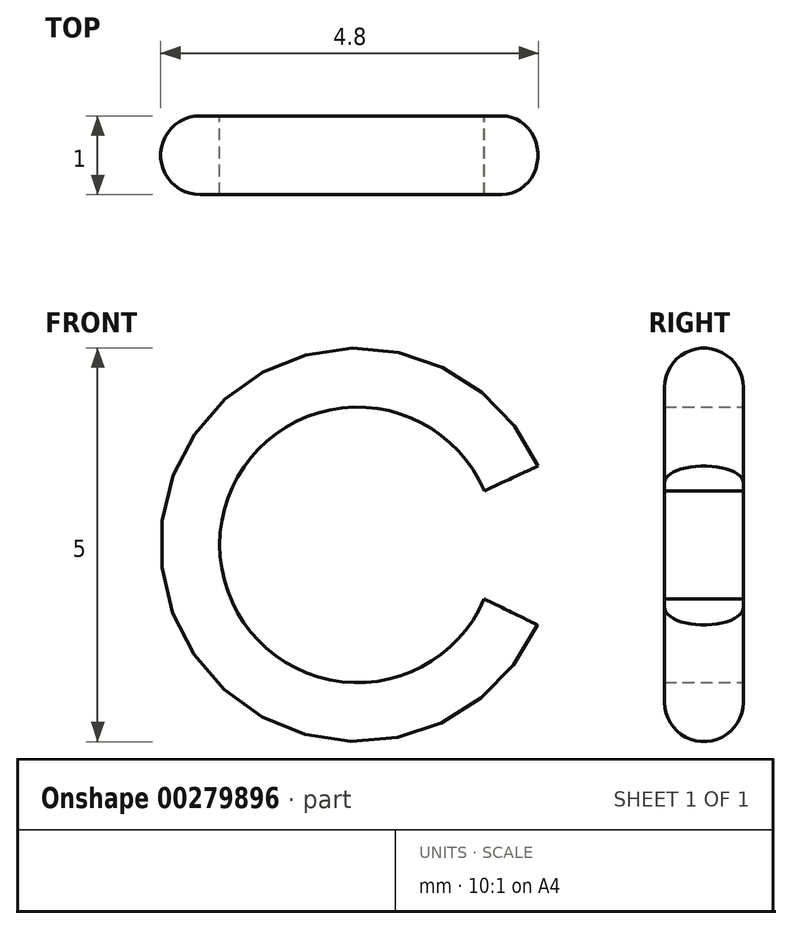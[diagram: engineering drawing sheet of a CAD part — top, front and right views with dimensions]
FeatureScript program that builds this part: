
annotation { "Feature Type Name" : "Feature", "Feature Type Description" : "" }
export const myFeature = defineFeature(function(context is Context, id is Id, definition is map)
    precondition{}
    {
        {
            var Q0;
            Q0=qCreatedBy(makeId("Front.planeOp"),FACE);
            var sketch = newSketch(context, id + "F0", { "sketchPlane" : qUnion([Q0])});
            skCircle(sketch, "E0", {"center": v(0, 0) * mm, "radius": 2.5 * mm});
            skCircle(sketch, "E1", {"center": v(0, 0) * mm, "radius": 1.75 * mm});
            skLineSegment(sketch, "E2", {"start": v(0, 0) * mm, "end": v(1.75, 0) * mm, "construction": true});
            skLineSegment(sketch, "E3", {"start": v(1.75, 0) * mm, "end": v(1.61, 0.69) * mm, "construction": true});
            skLineSegment(sketch, "E4", {"start": v(1.75, 0) * mm, "end": v(1.6, -0.69) * mm, "construction": true});
            skLineSegment(sketch, "E5", {"start": v(1.61, 0.69) * mm, "end": v(2.3, 1) * mm});
            skLineSegment(sketch, "E6", {"start": v(1.6, -0.69) * mm, "end": v(2.28, -1.02) * mm});
            skSolve(sketch);
        }
        {
            var Q0;
            Q0=makeQuery(id+"F0.imprint","IMPRINT",FACE,{"disambiguationData":[TD([[makeQuery(id+"F0.imprint","IMPRINT",EDGE,{"derivedFrom":sQuery(id+"F0.wireOp",EDGE,"E0")}),1.0]])]});
            var Q1;
            Q1=sQuery(id+"F0.wireOp",EDGE,"E0");
            extrude(context, id + "F1", {"entities" : qUnion([Q0]), "surfaceEntities" : qUnion([Q1]), "depth" : 1 * mm});
        }
        {
            var Q0;
            Q0=makeQuery(id+"F1.opExtrude","CAP_EDGE",EDGE,{"disambiguationData":[OSD([sQuery(id+"F0.wireOp",EDGE,"E0")])],"isStart":false});
            var Q1;
            Q1=makeQuery(id+"F1.opExtrude","CAP_EDGE",EDGE,{"disambiguationData":[OSD([sQuery(id+"F0.wireOp",EDGE,"E0")])],"isStart":true});
            fillet(context, id + "F2", {"entities" : qUnion([Q0, Q1]), "radius" : 0.5 * mm, "tangentPropagation" : true, "allowEdgeOverflow" : false});
        }
        {
            var Q0;
            {var subQ0=sQuery(id+"F0.wireOp",EDGE,"E5");Q0=makeQuery(id+"F0.imprint","IMPRINT",FACE,{"disambiguationData":[TD([[makeQuery(id+"F0.imprint","IMPRINT",EDGE,{"derivedFrom":subQ0}),-1.0]])]});}
            extrude(context, id + "F3", {"entities" : qUnion([Q0]), "operationType" : NewBodyOperationType.REMOVE, "depth" : 25 * mm});
        }
    });
